# Revit family: Kitchen_Taps-Mixers_hansgrohe_72808XXX-Talis-M54-Single-lever-kitchen-mixer-270-pull-out-spout-1jet
name_source: partatom
category: Plumbing Fixtures
revit_build: Autodesk Revit 2018 (Build: 20190510_1515(x64)
units: mm (PartAtom-declared; Revit-internal decimal feet)

## family parameters
Always vertical = No
Cut with Voids When Loaded = No
OmniClass Number = 23.31.11.00
OmniClass Title = Faucets
Part Type = Normal
Room Calculation Point = No
Round Connector Dimension = Use Diameter
Shared = No
Work Plane-Based = Yes

## types (4) — shared parameters
Always visible = Yes
BIMobject category = Taps & Mixers
Cold Water Inlet Description = Cold Water Inlet DN15
Cold Water Inlet Diameter = 9.525 mm  [stored 0.03125 ft]
Default Elevation = 1219.2 mm  [stored 4 ft]
Description = Talis M54 Single lever kitchen mixer 270, pull-out spout, 1jet
Edition number = 1
Hot Water Inlet Description = Hot Water Inlet DN15
Hot Water Inlet Diameter = 9.525 mm  [stored 0.03125 ft]
IFC Classification = Valve
Manufacturer = Hansgrohe
Manufacturer name = hansgrohe
Model = 72808XXX Talis M54 Single lever kitchen mixer 270, pull-out spout, 1jet
OmniClass Code = 23-31 11 00
OmniClass Description = Faucets
Product Guid = 41403f26-ad0d-478e-ae3b-47b7fc026c4a
Product SKU = 72808XXX
Product data url = https://bimobject.com
Product family = Talis M54
Product group = Kitchen mixers
Product name = 72808XXX Talis M54 Single lever kitchen mixer 270, pull-out spout, 1jet
Product url = https://www.hansgrohe.com
QR code = https://bimobject.com
URL = https://www.hansgrohe.com
Weight Net (Kg) = 2

## per-type parameters (varying)
| type | Main Material |
| 000 Chrome | Hansgrohe - Metal - 000 Chrome |
| 670 Matt Black | Hansgrohe - Metal - 670 Matt Black |
| 340 Brushed Black Chrome | Hansgrohe - Metal - 340 Brushed Black Chrome |
| 800 Stainless Steel Finish | Hansgrohe - Metal - 800 Stainless Steel Finish |

note: [stored X ft] marks values corroborated as IEEE doubles in the binary element streams (Revit-internal decimal feet)

## geometry (parser evidence)
native form markers: Sweep x4
no freeform markers — native parametric forms only
